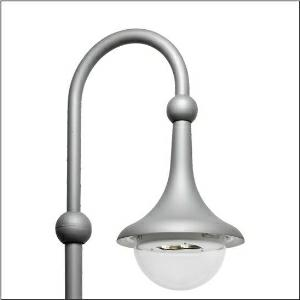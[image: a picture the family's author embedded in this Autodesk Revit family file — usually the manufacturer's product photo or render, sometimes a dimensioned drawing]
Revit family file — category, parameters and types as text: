
# Revit family: grosse_glocke_iq___st1_2a_5xa1565e1f108_d4d8
name_source: partatom
category: Lighting Fixtures
units: mm (PartAtom-declared; Revit-internal decimal feet)

## family parameters
Cut with Voids When Loaded = No
Host = Face
Light Source = No
Part Type = Normal
Room Calculation Point = No
Round Connector Dimension = Use Diameter
Shared = No

## types (1)
- --- (1 x LED, 5180 lm, 34.3 W, 3000K)
    Apparent Load = 34 VA
    CIE Flux Codes = 28 66 95 100 100
    Color Rendering = 70
    Color Temperature = 3000K
    Default Elevation = 1800 mm
    Description = Large Bell iQ, mast luminaire, primary light control with 3 zone facetted reflector, of plastic, silver coated, primary optical cover: enclosure, of PMMA, transparent, light distribution: ST1.2a, light emission: direct distribution, primary light characteristic: asymmetric, installation type: suspended mounting, High Power LED, rated luminous flux: 5.180lm, luminous efficacy: 151lm/W, light colour: 730, colour temperature: 3000K, control gear: iQ Street-Remote, control: optimised constant luminous flux control (CLO 2.0), Desk-Remote (wireless, voltage-free reading and setting of iQ features in the workshop via application-optimized NFC function/RFID function), Light-Fading, Smart-Wire, Night-Set, Lumen-Switch, Temp-Guard, Auto-Match, Street-Remote, pre-setting: logarithmic dimming characteristic, mains connection: 230..240V, AC, 50/60Hz, start of lifetime: 34W, end of service life: 38W, reduction: 16W, luminaire housing, bell-shaped, of glass-fibre reinforced polyester, coated, Siteco® metallic grey (DB 702S), please order curved mast extension separately, diameter: 530mm, height: 695mm, mounting height: 4..6m, protection rating (complete): IP54, insulation class (complete): insulation class II (safety insulation), certification: CE, ENEC, VDE, impact resistance: IK08, standard-compliant lighting for roads and squares, packaging unit: 1 piece

Light Distribution: ST1.2a
    Height = 695 mm
    Lamp = 1 x LED
    Lamp Light Flux = 5180 lm
    Lamp Power = 34.3 W
    Lamp count = 1
    Length = 530 mm
    Luminous efficacy = 151 lm/W
    Manufacturer = Siteco
    ModVariant = No
    Model = 5XA1565E1F108
    Number of Poles = 1
    OnlyDefault = Yes
    Power Factor = 1
    Product Name = Große Glocke iQ | ST1.2a
    Product group = mast luminaire | pylon annexe
    ProductGroupID = 6201
    Protection Class = Protection class II
    Protection Degree = IP 54
    RLX_Detail_Level = 1
    RLX_Emergency_Light_Flux = 0 lm
    RLX_Emergency_Type = 0
    RLX_Emergency_Type_DB = No
    RlxData = <blob elided: 85457 chars, md5=f345799e>
    Socket = socket
    Standby Power = 0 W
    System Light Flux = 5180 lm
    System Power = 34 W
    Type Comments = factory setting: luminous flux: 100 % | dim-lin: 254 | 640 mA
    Type Image = l_1347688.jpg
    URL = http://relux.com
    VarID = @adj_059816
    Voltage = 0 V
    Weight = 0.00 kg
    Width = 0 mm  [stored 0 ft]

note: [stored X ft] marks values corroborated as IEEE doubles in the binary element streams (Revit-internal decimal feet)

## geometry (parser evidence)
native form markers: Blend x4, Sweep x11
no freeform markers — native parametric forms only
